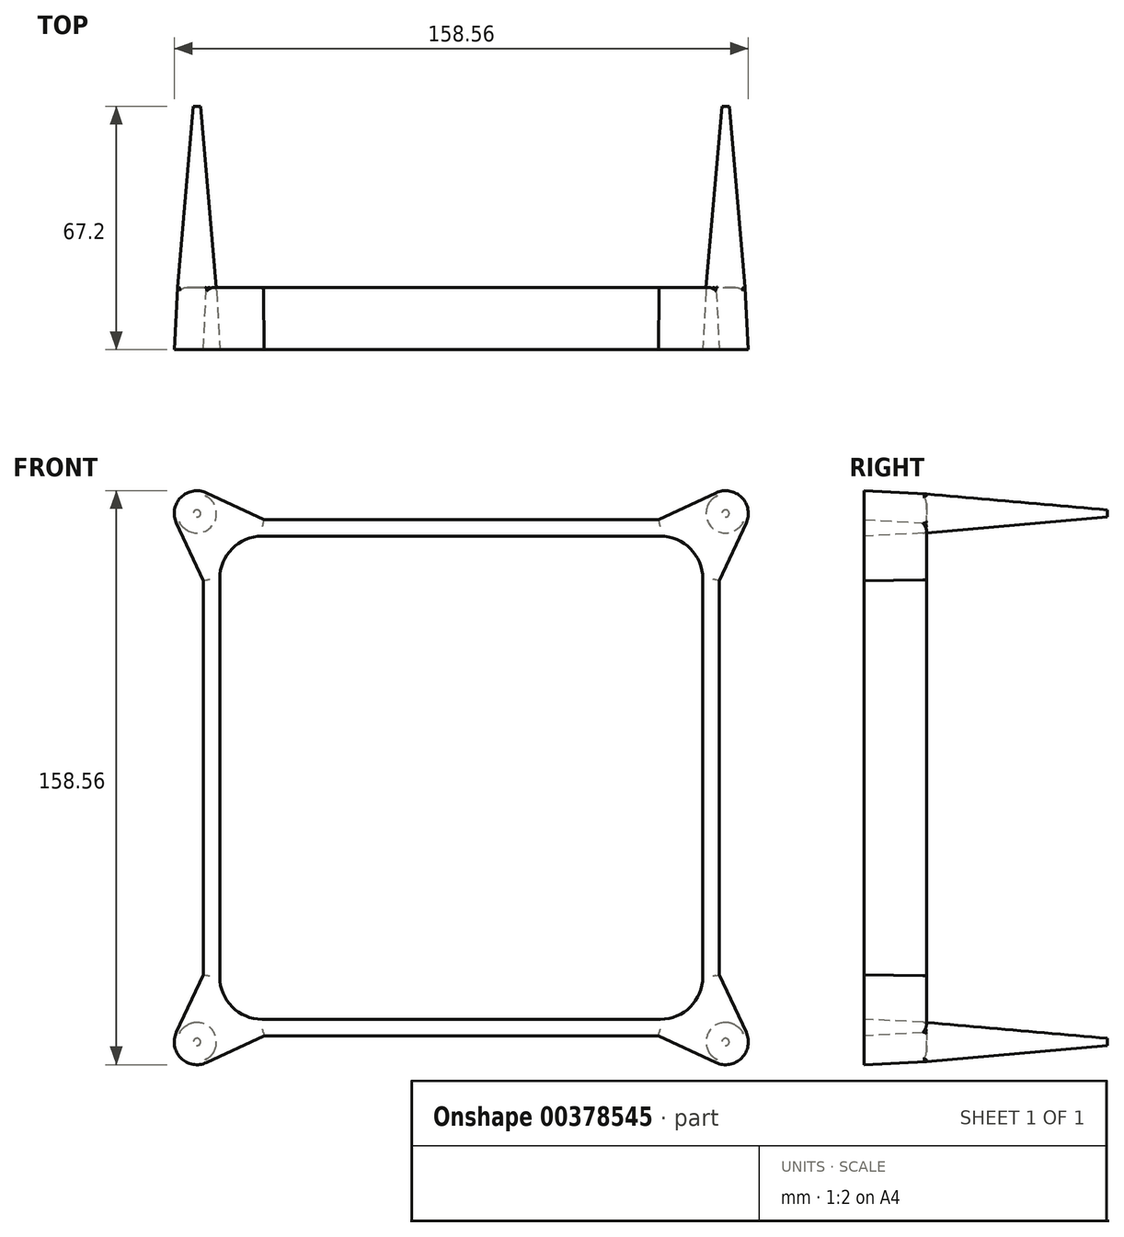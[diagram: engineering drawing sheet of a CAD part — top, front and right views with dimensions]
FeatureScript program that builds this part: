
annotation { "Feature Type Name" : "Feature", "Feature Type Description" : "" }
export const myFeature = defineFeature(function(context is Context, id is Id, definition is map)
    precondition{}
    {
        {
            var Q0;
            Q0=qCreatedBy(makeId("Front.planeOp"),FACE);
            var sketch = newSketch(context, id + "F0", { "sketchPlane" : qUnion([Q0])});
            skLineSegment(sketch, "E0.right", {"start": v(-73, 54.07) * mm, "end": v(-73, 0) * mm});
            skPoint(sketch, "E0.middle", {"position": v(0, 0) * mm});
            skLineSegment(sketch, "E1.bottom", {"start": v(0, 65) * mm, "end": v(-55, 65) * mm});
            skLineSegment(sketch, "E1.right", {"start": v(-65, 55) * mm, "end": v(-65, 0) * mm});
            skPoint(sketch, "E2.visualSharp", {"position": v(-65, 65) * mm});
            skArc(sketch, "E2.filletArc", {"start": v(-55, 65) * mm, "mid": v(-62.07, 62.07) * mm, "end": v(-65, 55) * mm});
            skPoint(sketch, "E3.visualSharp", {"position": v(-73, 73) * mm});
            skArc(sketch, "E4", {"start": v(-69.62, 80.25) * mm, "mid": v(-78.66, 78.66) * mm, "end": v(-80.25, 69.62) * mm});
            skLineSegment(sketch, "E5", {"start": v(-54.07, 73) * mm, "end": v(-69.62, 80.25) * mm});
            skLineSegment(sketch, "E6", {"start": v(-73, 54.07) * mm, "end": v(-80.25, 69.62) * mm});
            skLineSegment(sketch, "E7", {"start": v(-65, 0) * mm, "end": v(-73, 0) * mm});
            skLineSegment(sketch, "E8", {"start": v(0, 73) * mm, "end": v(0, 65) * mm});
            skLineSegment(sketch, "E9.trimOffspring", {"start": v(0, 73) * mm, "end": v(-54.07, 73) * mm});
            skLineSegment(sketch, "E10.MirrorCS", {"start": v(0, 73) * mm, "end": v(54.07, 73) * mm});
            skLineSegment(sketch, "E11.MirrorCS", {"start": v(65, 0) * mm, "end": v(73, 0) * mm});
            skLineSegment(sketch, "E12.MirrorCS", {"start": v(73, 54.07) * mm, "end": v(80.25, 69.62) * mm});
            skLineSegment(sketch, "E13.MirrorCS", {"start": v(54.07, 73) * mm, "end": v(69.62, 80.25) * mm});
            skLineSegment(sketch, "E14.MirrorCS", {"start": v(73, 54.07) * mm, "end": v(73, 0) * mm});
            skLineSegment(sketch, "E15.MirrorCS", {"start": v(65, 55) * mm, "end": v(65, 0) * mm});
            skLineSegment(sketch, "E16.MirrorCS", {"start": v(0, 65) * mm, "end": v(55, 65) * mm});
            skPoint(sketch, "E17.MirrorP", {"position": v(73, 73) * mm});
            skPoint(sketch, "E18.MirrorP", {"position": v(65, 65) * mm});
            skArc(sketch, "E19.MirrorCS", {"start": v(69.62, 80.25) * mm, "mid": v(78.66, 78.66) * mm, "end": v(80.25, 69.62) * mm});
            skArc(sketch, "E20.MirrorCS", {"start": v(55, 65) * mm, "mid": v(62.07, 62.07) * mm, "end": v(65, 55) * mm});
            skLineSegment(sketch, "E21.MirrorCS", {"start": v(65, -55) * mm, "end": v(65, 0) * mm});
            skLineSegment(sketch, "E22.MirrorCS", {"start": v(0, -73) * mm, "end": v(0, -65) * mm});
            skLineSegment(sketch, "E23.MirrorCS", {"start": v(0, -65) * mm, "end": v(-55, -65) * mm});
            skPoint(sketch, "E24.MirrorP", {"position": v(-73, -73) * mm});
            skArc(sketch, "E25.MirrorCS", {"start": v(-69.62, -80.25) * mm, "mid": v(-78.66, -78.66) * mm, "end": v(-80.25, -69.62) * mm});
            skLineSegment(sketch, "E26.MirrorCS", {"start": v(-65, -55) * mm, "end": v(-65, 0) * mm});
            skPoint(sketch, "E27.MirrorP", {"position": v(73, -73) * mm});
            skLineSegment(sketch, "E28.MirrorCS", {"start": v(0, -65) * mm, "end": v(55, -65) * mm});
            skLineSegment(sketch, "E29.MirrorCS", {"start": v(54.07, -73) * mm, "end": v(69.62, -80.25) * mm});
            skLineSegment(sketch, "E30.MirrorCS", {"start": v(-54.07, -73) * mm, "end": v(-69.62, -80.25) * mm});
            skArc(sketch, "E31.MirrorCS", {"start": v(69.62, -80.25) * mm, "mid": v(78.66, -78.66) * mm, "end": v(80.25, -69.62) * mm});
            skLineSegment(sketch, "E32.MirrorCS", {"start": v(-73, -54.07) * mm, "end": v(-73, 0) * mm});
            skArc(sketch, "E33.MirrorCS", {"start": v(-55, -65) * mm, "mid": v(-62.07, -62.07) * mm, "end": v(-65, -55) * mm});
            skLineSegment(sketch, "E34.MirrorCS", {"start": v(0, -73) * mm, "end": v(-54.07, -73) * mm});
            skPoint(sketch, "E35.MirrorP", {"position": v(65, -65) * mm});
            skLineSegment(sketch, "E36.MirrorCS", {"start": v(0, -73) * mm, "end": v(54.07, -73) * mm});
            skLineSegment(sketch, "E37.MirrorCS", {"start": v(-73, -54.07) * mm, "end": v(-80.25, -69.62) * mm});
            skArc(sketch, "E38.MirrorCS", {"start": v(55, -65) * mm, "mid": v(62.07, -62.07) * mm, "end": v(65, -55) * mm});
            skPoint(sketch, "E39.MirrorP", {"position": v(-65, -65) * mm});
            skLineSegment(sketch, "E40.MirrorCS", {"start": v(73, -54.07) * mm, "end": v(73, 0) * mm});
            skLineSegment(sketch, "E41.MirrorCS", {"start": v(73, -54.07) * mm, "end": v(80.25, -69.62) * mm});
            skSolve(sketch);
        }
        {
            var Q0;
            Q0=qSketchRegion(id+"F0",true);
            extrude(context, id + "F1", {"entities" : qUnion([Q0]), "oppositeDirection" : true, "depth" : 50 * mm, "hasDraft" : true, "draftAngle" : 3 * degree, "draftPullDirection" : true});
        }
        {
            var Q0;
            Q0=makeQuery(id+"F1.opExtrude","CAP_FACE",FACE,{"disambiguationData":[OSD([sQuery(id+"F0.wireOp",EDGE,"E0.right"),sQuery(id+"F0.wireOp",EDGE,"E1.bottom"),sQuery(id+"F0.wireOp",EDGE,"E1.right"),sQuery(id+"F0.wireOp",EDGE,"E2.filletArc"),sQuery(id+"F0.wireOp",EDGE,"E4"),sQuery(id+"F0.wireOp",EDGE,"E5"),sQuery(id+"F0.wireOp",EDGE,"E6"),sQuery(id+"F0.wireOp",EDGE,"E9.trimOffspring"),sQuery(id+"F0.wireOp",EDGE,"E10.MirrorCS"),sQuery(id+"F0.wireOp",EDGE,"E12.MirrorCS"),sQuery(id+"F0.wireOp",EDGE,"E13.MirrorCS"),sQuery(id+"F0.wireOp",EDGE,"E14.MirrorCS"),sQuery(id+"F0.wireOp",EDGE,"E15.MirrorCS"),sQuery(id+"F0.wireOp",EDGE,"E16.MirrorCS"),sQuery(id+"F0.wireOp",EDGE,"E19.MirrorCS"),sQuery(id+"F0.wireOp",EDGE,"E20.MirrorCS"),sQuery(id+"F0.wireOp",EDGE,"E21.MirrorCS"),sQuery(id+"F0.wireOp",EDGE,"E23.MirrorCS"),sQuery(id+"F0.wireOp",EDGE,"E25.MirrorCS"),sQuery(id+"F0.wireOp",EDGE,"E26.MirrorCS"),sQuery(id+"F0.wireOp",EDGE,"E28.MirrorCS"),sQuery(id+"F0.wireOp",EDGE,"E29.MirrorCS"),sQuery(id+"F0.wireOp",EDGE,"E30.MirrorCS"),sQuery(id+"F0.wireOp",EDGE,"E31.MirrorCS"),sQuery(id+"F0.wireOp",EDGE,"E32.MirrorCS"),sQuery(id+"F0.wireOp",EDGE,"E33.MirrorCS"),sQuery(id+"F0.wireOp",EDGE,"E34.MirrorCS"),sQuery(id+"F0.wireOp",EDGE,"E36.MirrorCS"),sQuery(id+"F0.wireOp",EDGE,"E37.MirrorCS"),sQuery(id+"F0.wireOp",EDGE,"E38.MirrorCS"),sQuery(id+"F0.wireOp",EDGE,"E40.MirrorCS"),sQuery(id+"F0.wireOp",EDGE,"E41.MirrorCS")])],"isStart":false});
            var sketch = newSketch(context, id + "F2", { "sketchPlane" : qUnion([Q0])});
            skCircle(sketch, "E42", {"center": v(-73, -73) * mm, "radius": 5.38 * mm});
            skCircle(sketch, "E43", {"center": v(73, -73) * mm, "radius": 5.38 * mm});
            skCircle(sketch, "E44", {"center": v(-73, 73) * mm, "radius": 5.38 * mm});
            skCircle(sketch, "E45", {"center": v(73, 73) * mm, "radius": 5.38 * mm});
            skSolve(sketch);
        }
        {
            var Q0;
            Q0=qSketchRegion(id+"F2",true);
            extrude(context, id + "F3", {"entities" : qUnion([Q0]), "operationType" : NewBodyOperationType.ADD, "depth" : 50 * mm, "hasDraft" : true, "draftAngle" : 5 * degree, "draftPullDirection" : true});
        }
        {
            var Q0;
            Q0=makeQuery(id+"F1.opExtrude","CAP_EDGE",EDGE,{"disambiguationData":[OSD([sQuery(id+"F0.wireOp",EDGE,"E23.MirrorCS"),sQuery(id+"F0.wireOp",EDGE,"E28.MirrorCS")])],"isStart":false});
            var Q1;
            Q1=makeQuery(id+"F1.opExtrude","CAP_EDGE",EDGE,{"disambiguationData":[OSD([sQuery(id+"F0.wireOp",EDGE,"E34.MirrorCS"),sQuery(id+"F0.wireOp",EDGE,"E36.MirrorCS")])],"isStart":false});
            var Q2;
            Q2=makeQuery(id+"F1.opExtrude","CAP_EDGE",EDGE,{"disambiguationData":[OSD([sQuery(id+"F0.wireOp",EDGE,"E30.MirrorCS")])],"isStart":false});
            var Q3;
            Q3=makeQuery(id+"F1.opExtrude","CAP_EDGE",EDGE,{"disambiguationData":[OSD([sQuery(id+"F0.wireOp",EDGE,"E0.right"),sQuery(id+"F0.wireOp",EDGE,"E32.MirrorCS")])],"isStart":false});
            var Q4;
            Q4=makeQuery(id+"F1.opExtrude","CAP_EDGE",EDGE,{"disambiguationData":[OSD([sQuery(id+"F0.wireOp",EDGE,"E6")])],"isStart":false});
            var Q5;
            Q5=makeQuery(id+"F1.opExtrude","CAP_EDGE",EDGE,{"disambiguationData":[OSD([sQuery(id+"F0.wireOp",EDGE,"E5")])],"isStart":false});
            var Q6;
            Q6=makeQuery(id+"F1.opExtrude","CAP_EDGE",EDGE,{"disambiguationData":[OSD([sQuery(id+"F0.wireOp",EDGE,"E9.trimOffspring"),sQuery(id+"F0.wireOp",EDGE,"E10.MirrorCS")])],"isStart":false});
            var Q7;
            Q7=makeQuery(id+"F1.opExtrude","CAP_EDGE",EDGE,{"disambiguationData":[OSD([sQuery(id+"F0.wireOp",EDGE,"E13.MirrorCS")])],"isStart":false});
            var Q8;
            Q8=makeQuery(id+"F1.opExtrude","CAP_EDGE",EDGE,{"disambiguationData":[OSD([sQuery(id+"F0.wireOp",EDGE,"E12.MirrorCS")])],"isStart":false});
            var Q9;
            Q9=makeQuery(id+"F1.opExtrude","CAP_EDGE",EDGE,{"disambiguationData":[OSD([sQuery(id+"F0.wireOp",EDGE,"E14.MirrorCS"),sQuery(id+"F0.wireOp",EDGE,"E40.MirrorCS")])],"isStart":false});
            var Q10;
            Q10=makeQuery(id+"F1.opExtrude","CAP_EDGE",EDGE,{"disambiguationData":[OSD([sQuery(id+"F0.wireOp",EDGE,"E29.MirrorCS")])],"isStart":false});
            var Q11;
            Q11=makeQuery(id+"F1.opExtrude","CAP_EDGE",EDGE,{"disambiguationData":[OSD([sQuery(id+"F0.wireOp",EDGE,"E41.MirrorCS")])],"isStart":false});
            var Q12;
            Q12=makeQuery(id+"F1.opExtrude","CAP_EDGE",EDGE,{"disambiguationData":[OSD([sQuery(id+"F0.wireOp",EDGE,"E37.MirrorCS")])],"isStart":false});
            fillet(context, id + "F4", {"entities" : qUnion([Q0, Q1, Q2, Q3, Q4, Q5, Q6, Q7, Q8, Q9, Q10, Q11, Q12]), "radius" : 1 * mm, "tangentPropagation" : true, "allowEdgeOverflow" : false});
        }
        {
            var Q0;
            Q0=makeQuery(id+"F1.opExtrude","CAP_FACE",FACE,{"disambiguationData":[OSD([sQuery(id+"F0.wireOp",EDGE,"E0.right"),sQuery(id+"F0.wireOp",EDGE,"E1.bottom"),sQuery(id+"F0.wireOp",EDGE,"E1.right"),sQuery(id+"F0.wireOp",EDGE,"E2.filletArc"),sQuery(id+"F0.wireOp",EDGE,"E4"),sQuery(id+"F0.wireOp",EDGE,"E5"),sQuery(id+"F0.wireOp",EDGE,"E6"),sQuery(id+"F0.wireOp",EDGE,"E9.trimOffspring"),sQuery(id+"F0.wireOp",EDGE,"E10.MirrorCS"),sQuery(id+"F0.wireOp",EDGE,"E12.MirrorCS"),sQuery(id+"F0.wireOp",EDGE,"E13.MirrorCS"),sQuery(id+"F0.wireOp",EDGE,"E14.MirrorCS"),sQuery(id+"F0.wireOp",EDGE,"E15.MirrorCS"),sQuery(id+"F0.wireOp",EDGE,"E16.MirrorCS"),sQuery(id+"F0.wireOp",EDGE,"E19.MirrorCS"),sQuery(id+"F0.wireOp",EDGE,"E20.MirrorCS"),sQuery(id+"F0.wireOp",EDGE,"E21.MirrorCS"),sQuery(id+"F0.wireOp",EDGE,"E23.MirrorCS"),sQuery(id+"F0.wireOp",EDGE,"E25.MirrorCS"),sQuery(id+"F0.wireOp",EDGE,"E26.MirrorCS"),sQuery(id+"F0.wireOp",EDGE,"E28.MirrorCS"),sQuery(id+"F0.wireOp",EDGE,"E29.MirrorCS"),sQuery(id+"F0.wireOp",EDGE,"E30.MirrorCS"),sQuery(id+"F0.wireOp",EDGE,"E31.MirrorCS"),sQuery(id+"F0.wireOp",EDGE,"E32.MirrorCS"),sQuery(id+"F0.wireOp",EDGE,"E33.MirrorCS"),sQuery(id+"F0.wireOp",EDGE,"E34.MirrorCS"),sQuery(id+"F0.wireOp",EDGE,"E36.MirrorCS"),sQuery(id+"F0.wireOp",EDGE,"E37.MirrorCS"),sQuery(id+"F0.wireOp",EDGE,"E38.MirrorCS"),sQuery(id+"F0.wireOp",EDGE,"E40.MirrorCS"),sQuery(id+"F0.wireOp",EDGE,"E41.MirrorCS")])],"isStart":true});
            var sketch = newSketch(context, id + "F5", { "sketchPlane" : qUnion([Q0])});
            skPoint(sketch, "E46.firstSnap0", {"position": v(-61.84, 76.63) * mm});
            skLineSegment(sketch, "E46.bottom", {"start": v(-2.5, 78) * mm, "end": v(2.5, 78) * mm});
            skLineSegment(sketch, "E46.top", {"start": v(-2.5, -78) * mm, "end": v(2.5, -78) * mm});
            skLineSegment(sketch, "E46.left", {"start": v(-2.5, 78) * mm, "end": v(-2.5, 9.68) * mm});
            skLineSegment(sketch, "E46.right", {"start": v(2.5, 78) * mm, "end": v(2.5, 9.68) * mm});
            skLineSegment(sketch, "E47.bottom", {"start": v(-78, 2.5) * mm, "end": v(-9.68, 2.5) * mm});
            skLineSegment(sketch, "E47.top", {"start": v(-78, -2.5) * mm, "end": v(-9.68, -2.5) * mm});
            skLineSegment(sketch, "E47.left", {"start": v(-78, 2.5) * mm, "end": v(-78, -2.5) * mm});
            skLineSegment(sketch, "E47.right", {"start": v(78, 2.5) * mm, "end": v(78, -2.5) * mm});
            skArc(sketch, "E48", {"start": v(-2.5, 9.68) * mm, "mid": v(-7.07, 7.07) * mm, "end": v(-9.68, 2.5) * mm});
            skLineSegment(sketch, "E49.trimOffspring", {"start": v(9.68, 2.5) * mm, "end": v(78, 2.5) * mm});
            skLineSegment(sketch, "E50.trimOffspring", {"start": v(9.68, -2.5) * mm, "end": v(78, -2.5) * mm});
            skLineSegment(sketch, "E51.trimOffspring", {"start": v(2.5, -9.68) * mm, "end": v(2.5, -78) * mm});
            skLineSegment(sketch, "E52.trimOffspring", {"start": v(-2.5, -9.68) * mm, "end": v(-2.5, -78) * mm});
            skArc(sketch, "E53.trimOffspring", {"start": v(-9.68, -2.5) * mm, "mid": v(-7.07, -7.07) * mm, "end": v(-2.5, -9.68) * mm});
            skArc(sketch, "E54.trimOffspring", {"start": v(2.5, -9.68) * mm, "mid": v(7.07, -7.07) * mm, "end": v(9.68, -2.5) * mm});
            skArc(sketch, "E55.trimOffspring", {"start": v(9.68, 2.5) * mm, "mid": v(7.07, 7.07) * mm, "end": v(2.5, 9.68) * mm});
            skCircle(sketch, "E56", {"center": v(0, 0) * mm, "radius": 1.5 * mm});
            skSolve(sketch);
        }
        {
            var Q0;
            Q0=qSketchRegion(id+"F5",true);
            extrude(context, id + "F6", {"entities" : qUnion([Q0]), "depth" : 10 * mm});
        }
        {
            var Q0;
            Q0=makeQuery(id+"F6.opExtrude","CAP_FACE",FACE,{"disambiguationData":[OSD([sQuery(id+"F5.wireOp",EDGE,"E46.bottom"),sQuery(id+"F5.wireOp",EDGE,"E46.top"),sQuery(id+"F5.wireOp",EDGE,"E46.left"),sQuery(id+"F5.wireOp",EDGE,"E46.right"),sQuery(id+"F5.wireOp",EDGE,"E47.bottom"),sQuery(id+"F5.wireOp",EDGE,"E47.top"),sQuery(id+"F5.wireOp",EDGE,"E47.left"),sQuery(id+"F5.wireOp",EDGE,"E47.right"),sQuery(id+"F5.wireOp",EDGE,"E48"),sQuery(id+"F5.wireOp",EDGE,"E49.trimOffspring"),sQuery(id+"F5.wireOp",EDGE,"E50.trimOffspring"),sQuery(id+"F5.wireOp",EDGE,"E51.trimOffspring"),sQuery(id+"F5.wireOp",EDGE,"E52.trimOffspring"),sQuery(id+"F5.wireOp",EDGE,"E53.trimOffspring"),sQuery(id+"F5.wireOp",EDGE,"E54.trimOffspring"),sQuery(id+"F5.wireOp",EDGE,"E55.trimOffspring"),sQuery(id+"F5.wireOp",EDGE,"E56")])],"isStart":true});
            var sketch = newSketch(context, id + "F7", { "sketchPlane" : qUnion([Q0])});
            skLineSegment(sketch, "E57.bottom", {"start": v(78, 5) * mm, "end": v(73.5, 5) * mm});
            skLineSegment(sketch, "E57.top", {"start": v(78, -5) * mm, "end": v(73.5, -5) * mm});
            skLineSegment(sketch, "E57.left", {"start": v(78, 5) * mm, "end": v(78, -5) * mm});
            skLineSegment(sketch, "E57.right", {"start": v(73.5, 5) * mm, "end": v(73.5, -5) * mm});
            skLineSegment(sketch, "E58.bottom", {"start": v(5, -73.5) * mm, "end": v(-5, -73.5) * mm});
            skLineSegment(sketch, "E58.top", {"start": v(5, -78) * mm, "end": v(-5, -78) * mm});
            skLineSegment(sketch, "E58.left", {"start": v(5, -73.5) * mm, "end": v(5, -78) * mm});
            skLineSegment(sketch, "E58.right", {"start": v(-5, -73.5) * mm, "end": v(-5, -78) * mm});
            skLineSegment(sketch, "E59.bottom", {"start": v(-78, -5) * mm, "end": v(-73.5, -5) * mm});
            skLineSegment(sketch, "E59.top", {"start": v(-78, 5) * mm, "end": v(-73.5, 5) * mm});
            skLineSegment(sketch, "E59.left", {"start": v(-78, -5) * mm, "end": v(-78, 5) * mm});
            skLineSegment(sketch, "E59.right", {"start": v(-73.5, -5) * mm, "end": v(-73.5, 5) * mm});
            skLineSegment(sketch, "E60.bottom", {"start": v(-5, 73.5) * mm, "end": v(5, 73.5) * mm});
            skLineSegment(sketch, "E60.top", {"start": v(-5, 78) * mm, "end": v(5, 78) * mm});
            skLineSegment(sketch, "E60.left", {"start": v(-5, 73.5) * mm, "end": v(-5, 78) * mm});
            skLineSegment(sketch, "E60.right", {"start": v(5, 73.5) * mm, "end": v(5, 78) * mm});
            skSolve(sketch);
        }
        {
            var Q0;
            Q0=qSketchRegion(id+"F7",true);
            extrude(context, id + "F8", {"entities" : qUnion([Q0]), "operationType" : NewBodyOperationType.ADD, "depth" : 5 * mm});
        }
        {
            var Q0;
            {var subQ0=sQuery(id+"F5.wireOp",EDGE,"E49.trimOffspring");Q0=makeQuery(id+"F8.boolean.opBoolean","SPLIT",EDGE,{"disambiguationData":[topologyDisambiguationEdgeConnected([makeQuery(id+"F8.opExtrude","CAP_FACE",FACE,{"disambiguationData":[OSD([sQuery(id+"F7.wireOp",EDGE,"E59.bottom"),sQuery(id+"F7.wireOp",EDGE,"E59.top"),sQuery(id+"F7.wireOp",EDGE,"E59.left"),sQuery(id+"F7.wireOp",EDGE,"E59.right")])],"isStart":true})])],"derivedFrom":makeQuery(id+"F6.opExtrude","CAP_EDGE",EDGE,{"disambiguationData":[OSD([subQ0])],"isStart":true})});}
            var Q1;
            {var subQ0=sQuery(id+"F5.wireOp",EDGE,"E50.trimOffspring");Q1=makeQuery(id+"F8.boolean.opBoolean","SPLIT",EDGE,{"disambiguationData":[topologyDisambiguationEdgeConnected([makeQuery(id+"F8.opExtrude","CAP_FACE",FACE,{"disambiguationData":[OSD([sQuery(id+"F7.wireOp",EDGE,"E59.bottom"),sQuery(id+"F7.wireOp",EDGE,"E59.top"),sQuery(id+"F7.wireOp",EDGE,"E59.left"),sQuery(id+"F7.wireOp",EDGE,"E59.right")])],"isStart":true})])],"derivedFrom":makeQuery(id+"F6.opExtrude","CAP_EDGE",EDGE,{"disambiguationData":[OSD([subQ0])],"isStart":true})});}
            var Q2;
            {var subQ0=sQuery(id+"F5.wireOp",EDGE,"E46.right");Q2=makeQuery(id+"F8.boolean.opBoolean","SPLIT",EDGE,{"disambiguationData":[topologyDisambiguationEdgeConnected([makeQuery(id+"F8.opExtrude","CAP_FACE",FACE,{"disambiguationData":[OSD([sQuery(id+"F7.wireOp",EDGE,"E60.bottom"),sQuery(id+"F7.wireOp",EDGE,"E60.top"),sQuery(id+"F7.wireOp",EDGE,"E60.left"),sQuery(id+"F7.wireOp",EDGE,"E60.right")])],"isStart":true})])],"derivedFrom":makeQuery(id+"F6.opExtrude","CAP_EDGE",EDGE,{"disambiguationData":[OSD([subQ0])],"isStart":true})});}
            var Q3;
            {var subQ0=sQuery(id+"F5.wireOp",EDGE,"E46.left");Q3=makeQuery(id+"F8.boolean.opBoolean","SPLIT",EDGE,{"disambiguationData":[topologyDisambiguationEdgeConnected([makeQuery(id+"F8.opExtrude","CAP_FACE",FACE,{"disambiguationData":[OSD([sQuery(id+"F7.wireOp",EDGE,"E60.bottom"),sQuery(id+"F7.wireOp",EDGE,"E60.top"),sQuery(id+"F7.wireOp",EDGE,"E60.left"),sQuery(id+"F7.wireOp",EDGE,"E60.right")])],"isStart":true})])],"derivedFrom":makeQuery(id+"F6.opExtrude","CAP_EDGE",EDGE,{"disambiguationData":[OSD([subQ0])],"isStart":true})});}
            var Q4;
            {var subQ0=sQuery(id+"F5.wireOp",EDGE,"E47.top");Q4=makeQuery(id+"F8.boolean.opBoolean","SPLIT",EDGE,{"disambiguationData":[topologyDisambiguationEdgeConnected([makeQuery(id+"F8.opExtrude","CAP_FACE",FACE,{"disambiguationData":[OSD([sQuery(id+"F7.wireOp",EDGE,"E57.bottom"),sQuery(id+"F7.wireOp",EDGE,"E57.top"),sQuery(id+"F7.wireOp",EDGE,"E57.left"),sQuery(id+"F7.wireOp",EDGE,"E57.right")])],"isStart":true})])],"derivedFrom":makeQuery(id+"F6.opExtrude","CAP_EDGE",EDGE,{"disambiguationData":[OSD([subQ0])],"isStart":true})});}
            var Q5;
            {var subQ0=sQuery(id+"F5.wireOp",EDGE,"E47.bottom");Q5=makeQuery(id+"F8.boolean.opBoolean","SPLIT",EDGE,{"disambiguationData":[topologyDisambiguationEdgeConnected([makeQuery(id+"F8.opExtrude","CAP_FACE",FACE,{"disambiguationData":[OSD([sQuery(id+"F7.wireOp",EDGE,"E57.bottom"),sQuery(id+"F7.wireOp",EDGE,"E57.top"),sQuery(id+"F7.wireOp",EDGE,"E57.left"),sQuery(id+"F7.wireOp",EDGE,"E57.right")])],"isStart":true})])],"derivedFrom":makeQuery(id+"F6.opExtrude","CAP_EDGE",EDGE,{"disambiguationData":[OSD([subQ0])],"isStart":true})});}
            var Q6;
            {var subQ0=sQuery(id+"F5.wireOp",EDGE,"E52.trimOffspring");Q6=makeQuery(id+"F8.boolean.opBoolean","SPLIT",EDGE,{"disambiguationData":[topologyDisambiguationEdgeConnected([makeQuery(id+"F8.opExtrude","CAP_FACE",FACE,{"disambiguationData":[OSD([sQuery(id+"F7.wireOp",EDGE,"E58.bottom"),sQuery(id+"F7.wireOp",EDGE,"E58.top"),sQuery(id+"F7.wireOp",EDGE,"E58.left"),sQuery(id+"F7.wireOp",EDGE,"E58.right")])],"isStart":true})])],"derivedFrom":makeQuery(id+"F6.opExtrude","CAP_EDGE",EDGE,{"disambiguationData":[OSD([subQ0])],"isStart":true})});}
            var Q7;
            {var subQ0=sQuery(id+"F5.wireOp",EDGE,"E51.trimOffspring");Q7=makeQuery(id+"F8.boolean.opBoolean","SPLIT",EDGE,{"disambiguationData":[topologyDisambiguationEdgeConnected([makeQuery(id+"F8.opExtrude","CAP_FACE",FACE,{"disambiguationData":[OSD([sQuery(id+"F7.wireOp",EDGE,"E58.bottom"),sQuery(id+"F7.wireOp",EDGE,"E58.top"),sQuery(id+"F7.wireOp",EDGE,"E58.left"),sQuery(id+"F7.wireOp",EDGE,"E58.right")])],"isStart":true})])],"derivedFrom":makeQuery(id+"F6.opExtrude","CAP_EDGE",EDGE,{"disambiguationData":[OSD([subQ0])],"isStart":true})});}
            chamfer(context, id + "F9", {"entities" : qUnion([Q0, Q1, Q2, Q3, Q4, Q5, Q6, Q7]), "width" : 2.5 * mm, "tangentPropagation" : true});
        }
        {
            var Q0;
            Q0=makeQuery(id+"F6.opExtrude","CAP_EDGE",EDGE,{"disambiguationData":[OSD([sQuery(id+"F5.wireOp",EDGE,"E46.bottom")])],"isStart":false});
            var Q1;
            Q1=makeQuery(id+"F6.opExtrude","CAP_EDGE",EDGE,{"disambiguationData":[OSD([sQuery(id+"F5.wireOp",EDGE,"E47.left")])],"isStart":false});
            var Q2;
            Q2=makeQuery(id+"F6.opExtrude","CAP_EDGE",EDGE,{"disambiguationData":[OSD([sQuery(id+"F5.wireOp",EDGE,"E46.top")])],"isStart":false});
            var Q3;
            Q3=makeQuery(id+"F6.opExtrude","CAP_EDGE",EDGE,{"disambiguationData":[OSD([sQuery(id+"F5.wireOp",EDGE,"E47.right")])],"isStart":false});
            chamfer(context, id + "F10", {"entities" : qUnion([Q0, Q1, Q2, Q3]), "width" : 5 * mm, "tangentPropagation" : true});
        }
        {
            var Q0;
            Q0=makeQuery(id+"F6.opExtrude","SWEPT_BODY",BODY,{"disambiguationData":[OSD([sQuery(id+"F5.wireOp",EDGE,"E46.bottom"),sQuery(id+"F5.wireOp",EDGE,"E46.top"),sQuery(id+"F5.wireOp",EDGE,"E46.left"),sQuery(id+"F5.wireOp",EDGE,"E46.right"),sQuery(id+"F5.wireOp",EDGE,"E47.bottom"),sQuery(id+"F5.wireOp",EDGE,"E47.top"),sQuery(id+"F5.wireOp",EDGE,"E47.left"),sQuery(id+"F5.wireOp",EDGE,"E47.right"),sQuery(id+"F5.wireOp",EDGE,"E48"),sQuery(id+"F5.wireOp",EDGE,"E49.trimOffspring"),sQuery(id+"F5.wireOp",EDGE,"E50.trimOffspring"),sQuery(id+"F5.wireOp",EDGE,"E51.trimOffspring"),sQuery(id+"F5.wireOp",EDGE,"E52.trimOffspring"),sQuery(id+"F5.wireOp",EDGE,"E53.trimOffspring"),sQuery(id+"F5.wireOp",EDGE,"E54.trimOffspring"),sQuery(id+"F5.wireOp",EDGE,"E55.trimOffspring"),sQuery(id+"F5.wireOp",EDGE,"E56")])]});
            deleteBodies(context, id + "F11", {"entities" : qUnion([Q0])});
        }
        {
            var Q0;
            Q0=qCreatedBy(makeId("Right.planeOp"),FACE);
            var sketch = newSketch(context, id + "F12", { "sketchPlane" : qUnion([Q0])});
            skLineSegment(sketch, "E61.bottom", {"start": v(0, 92.85) * mm, "end": v(32.8, 92.85) * mm});
            skLineSegment(sketch, "E61.top", {"start": v(0, -101.35) * mm, "end": v(32.8, -101.35) * mm});
            skLineSegment(sketch, "E61.left", {"start": v(0, 92.85) * mm, "end": v(0, -101.35) * mm});
            skLineSegment(sketch, "E61.right", {"start": v(32.8, 92.85) * mm, "end": v(32.8, -101.35) * mm});
            skSolve(sketch);
        }
        {
            var Q0;
            Q0 = qSketchRegion(id + "F12", true);
            extrude(context, id + "F13", {"entities" : qUnion([Q0]), "operationType" : NewBodyOperationType.REMOVE, "depth" : 200 * mm, "symmetric" : true});
        }
    });
